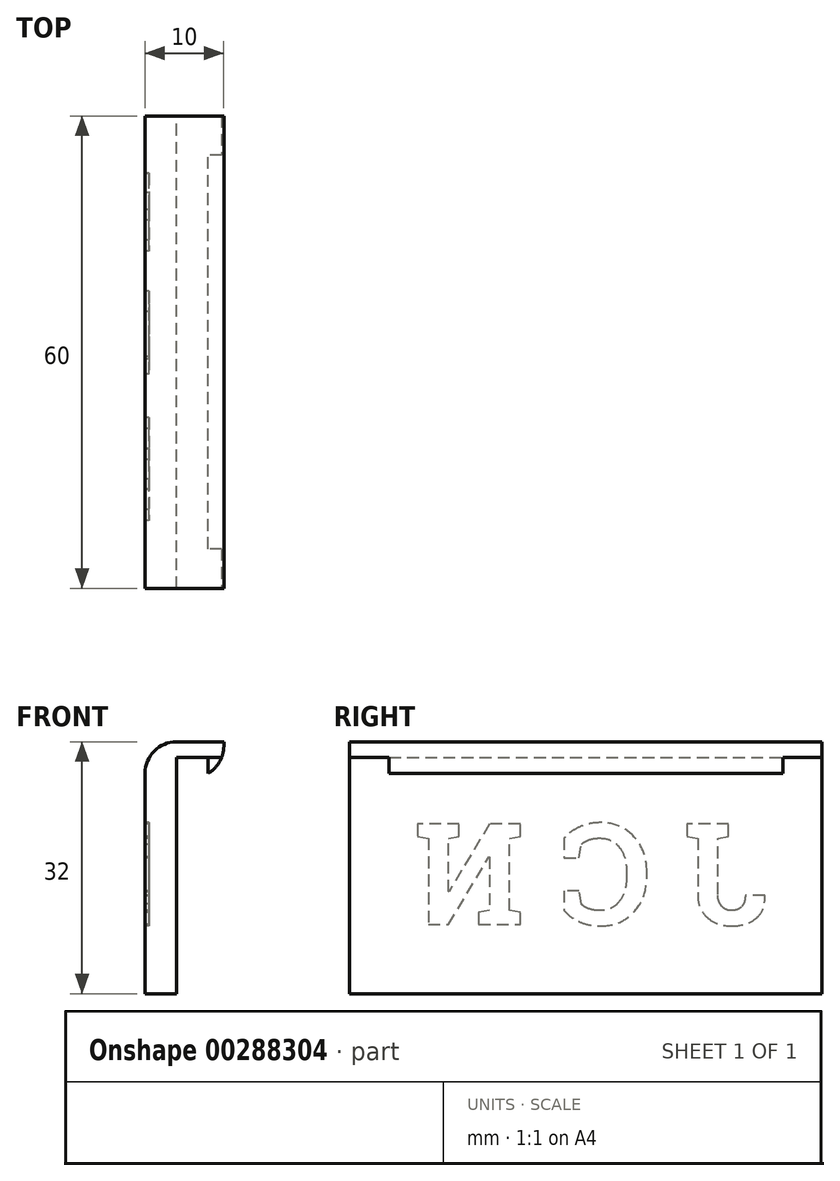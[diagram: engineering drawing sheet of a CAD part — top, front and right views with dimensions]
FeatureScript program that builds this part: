
annotation { "Feature Type Name" : "Feature", "Feature Type Description" : "" }
export const myFeature = defineFeature(function(context is Context, id is Id, definition is map)
    precondition{}
    {
        {
            var Q0;
            Q0=qCreatedBy(makeId("Front.planeOp"),FACE);
            var sketch = newSketch(context, id + "F0", { "sketchPlane" : qUnion([Q0])});
            skLineSegment(sketch, "E0", {"start": v(4.5, 0) * mm, "end": v(4.5, 0) * mm});
            skLineSegment(sketch, "E1", {"start": v(4.5, 0) * mm, "end": v(0.5, 0) * mm});
            skLineSegment(sketch, "E2", {"start": v(0.5, 0) * mm, "end": v(0.5, -30) * mm});
            skLineSegment(sketch, "E3", {"start": v(4.5, 0) * mm, "end": v(6.5, 0) * mm});
            skLineSegment(sketch, "E4", {"start": v(6.5, 0) * mm, "end": v(6.5, 2) * mm});
            skLineSegment(sketch, "E5", {"start": v(6.5, 2) * mm, "end": v(-3.5, 2) * mm});
            skLineSegment(sketch, "E6", {"start": v(-3.5, 2) * mm, "end": v(-3.5, -30) * mm});
            skLineSegment(sketch, "E7", {"start": v(-3.5, -30) * mm, "end": v(0.5, -30) * mm});
            skSolve(sketch);
        }
        {
            var Q0;
            Q0=makeQuery(id+"F0.imprint","IMPRINT",FACE,{"disambiguationData":[TD([[makeQuery(id+"F0.imprint","IMPRINT",EDGE,{"derivedFrom":sQuery(id+"F0.wireOp",EDGE,"E1")}),-1.0]])]});
            extrude(context, id + "F1", {"entities" : qUnion([Q0]), "depth" : 60 * mm});
        }
        {
            var Q0;
            Q0=makeQuery(id+"F1.opExtrude","SWEPT_EDGE",EDGE,{"disambiguationData":[OSD([sQuery(id+"F0.wireOp",EDGE,"E5"),sQuery(id+"F0.wireOp",EDGE,"E6")])]});
            fillet(context, id + "F2", {"entities" : qUnion([Q0]), "radius" : 4 * mm, "tangentPropagation" : true, "allowEdgeOverflow" : false});
        }
        {
            var Q0;
            Q0=makeQuery(id+"F1.opExtrude","SWEPT_FACE",FACE,{"disambiguationData":[OSD([sQuery(id+"F0.wireOp",EDGE,"E1"),sQuery(id+"F0.wireOp",EDGE,"E3")])]});
            var sketch = newSketch(context, id + "F3", { "sketchPlane" : qUnion([Q0])});
            skLineSegment(sketch, "E8.bottom", {"start": v(6.5, 55) * mm, "end": v(4.5, 55) * mm});
            skLineSegment(sketch, "E8.top", {"start": v(6.5, 5) * mm, "end": v(4.5, 5) * mm});
            skLineSegment(sketch, "E8.left", {"start": v(6.5, 55) * mm, "end": v(6.5, 5) * mm});
            skLineSegment(sketch, "E8.right", {"start": v(4.5, 55) * mm, "end": v(4.5, 5) * mm});
            skSolve(sketch);
        }
        {
            var Q0;
            Q0=makeQuery(id+"F3.imprint","IMPRINT",FACE,{"disambiguationData":[TD([[makeQuery(id+"F3.imprint","IMPRINT",EDGE,{"derivedFrom":sQuery(id+"F3.wireOp",EDGE,"E8.bottom")}),1.0]])]});
            extrude(context, id + "F4", {"entities" : qUnion([Q0]), "operationType" : NewBodyOperationType.ADD, "depth" : 2 * mm});
        }
        {
            var Q0;
            Q0=makeQuery(id+"F4.opExtrude","CAP_EDGE",EDGE,{"disambiguationData":[OSD([sQuery(id+"F3.wireOp",EDGE,"E8.left")])],"isStart":false});
            fillet(context, id + "F5", {"entities" : qUnion([Q0]), "radius" : 4 * mm, "tangentPropagation" : true, "allowEdgeOverflow" : false});
        }
        {
            var Q0;
            Q0=makeQuery(id+"F1.opExtrude","SWEPT_FACE",FACE,{"disambiguationData":[OSD([sQuery(id+"F0.wireOp",EDGE,"E6")])]});
            var sketch = newSketch(context, id + "F6", { "sketchPlane" : qUnion([Q0])});
            skText(sketch, "E9", { "text": "J C N", "fontName": "RobotoSlab-Bold.ttf"});
            const initialGuessF6  = {"E9": [0.00695, -0.02122, 1, 0, 0.01293]};
            skSetInitialGuess(sketch, initialGuessF6);
            skSolve(sketch);
        }
        {
            var Q0;
            Q0 = qSketchRegion(id + "F6", true);
            extrude(context, id + "F7", {"entities" : qUnion([Q0]), "operationType" : NewBodyOperationType.REMOVE, "oppositeDirection" : true, "depth" : 0.5 * mm});
        }
    });
